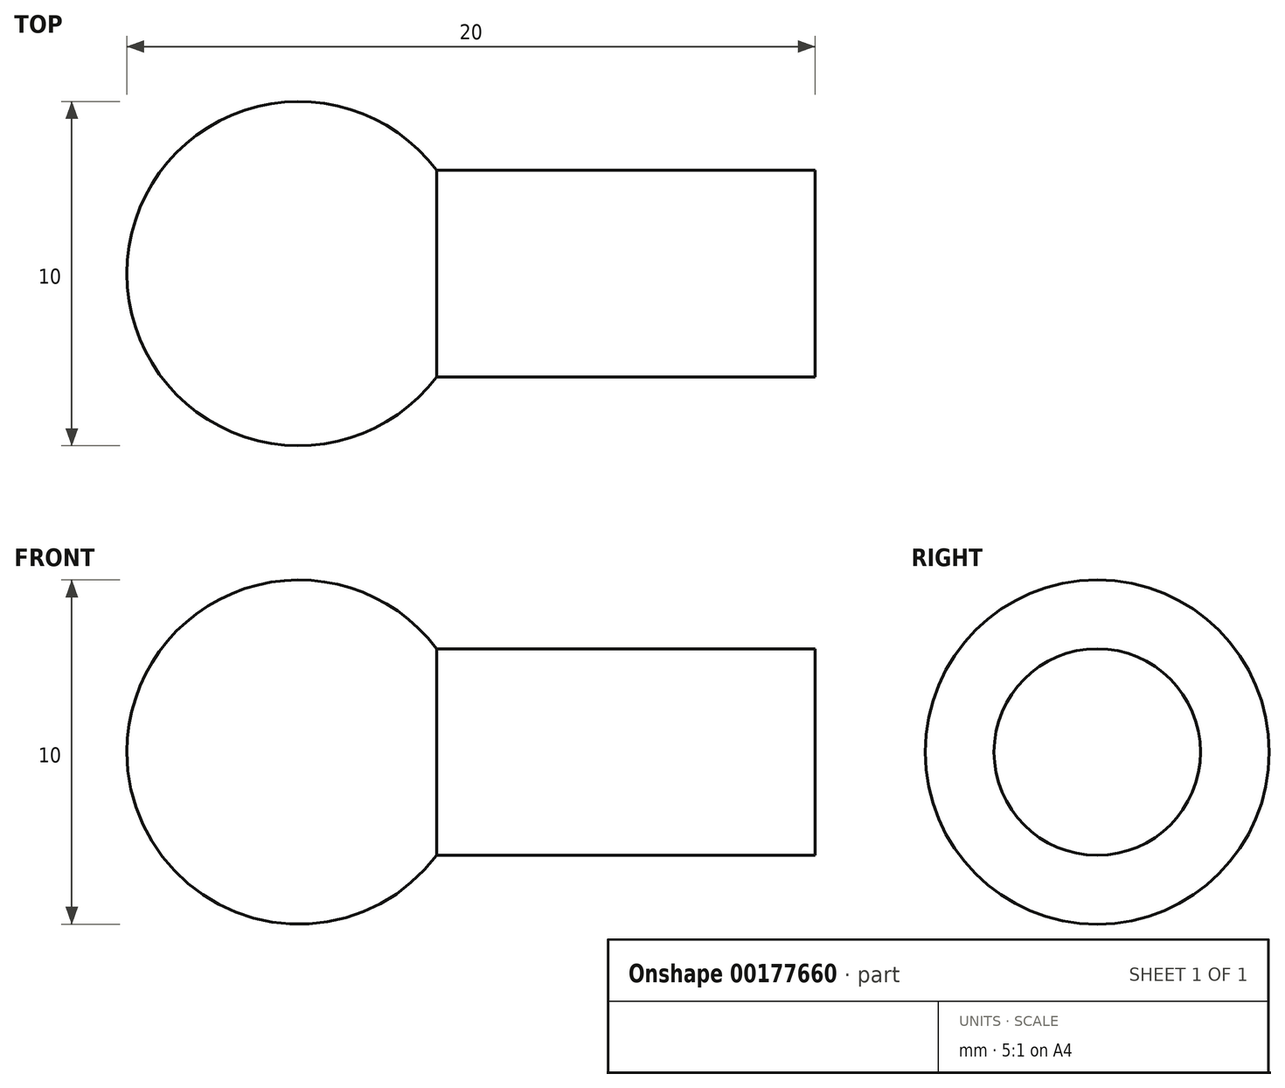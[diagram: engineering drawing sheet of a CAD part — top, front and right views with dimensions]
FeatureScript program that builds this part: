
annotation { "Feature Type Name" : "Feature", "Feature Type Description" : "" }
export const myFeature = defineFeature(function(context is Context, id is Id, definition is map)
    precondition{}
    {
        {
            var Q0;
            Q0=qCreatedBy(makeId("Front.planeOp"),FACE);
            var sketch = newSketch(context, id + "F0", { "sketchPlane" : qUnion([Q0])});
            skLineSegment(sketch, "E0", {"start": v(0, 0) * mm, "end": v(-18.8, 0) * mm});
            skLineSegment(sketch, "E1", {"start": v(0, 0) * mm, "end": v(0, -3) * mm});
            skLineSegment(sketch, "E2.0", {"start": v(0, -3) * mm, "end": v(-11, -3) * mm});
            skArc(sketch, "E3", {"start": v(-18.8, -3.24) * mm, "mid": v(-14.85, -5) * mm, "end": v(-11, -3) * mm});
            skArc(sketch, "E4", {"start": v(-20, 0) * mm, "mid": v(-16.58, -4.74) * mm, "end": v(-11, -3) * mm});
            skLineSegment(sketch, "E5", {"start": v(-18.8, 0) * mm, "end": v(-20, 0) * mm});
            skSolve(sketch);
        }
        {
            var Q0;
            Q0=qSketchRegion(id+"F0",true);
            var Q1;
            Q1=sQuery(id+"F0.wireOp",EDGE,"E0");
            revolve(context, id + "F1", {"entities" : qUnion([Q0]), "axis" : qUnion([Q1]), "revolveType" : RevolveType.FULL});
        }
    });
